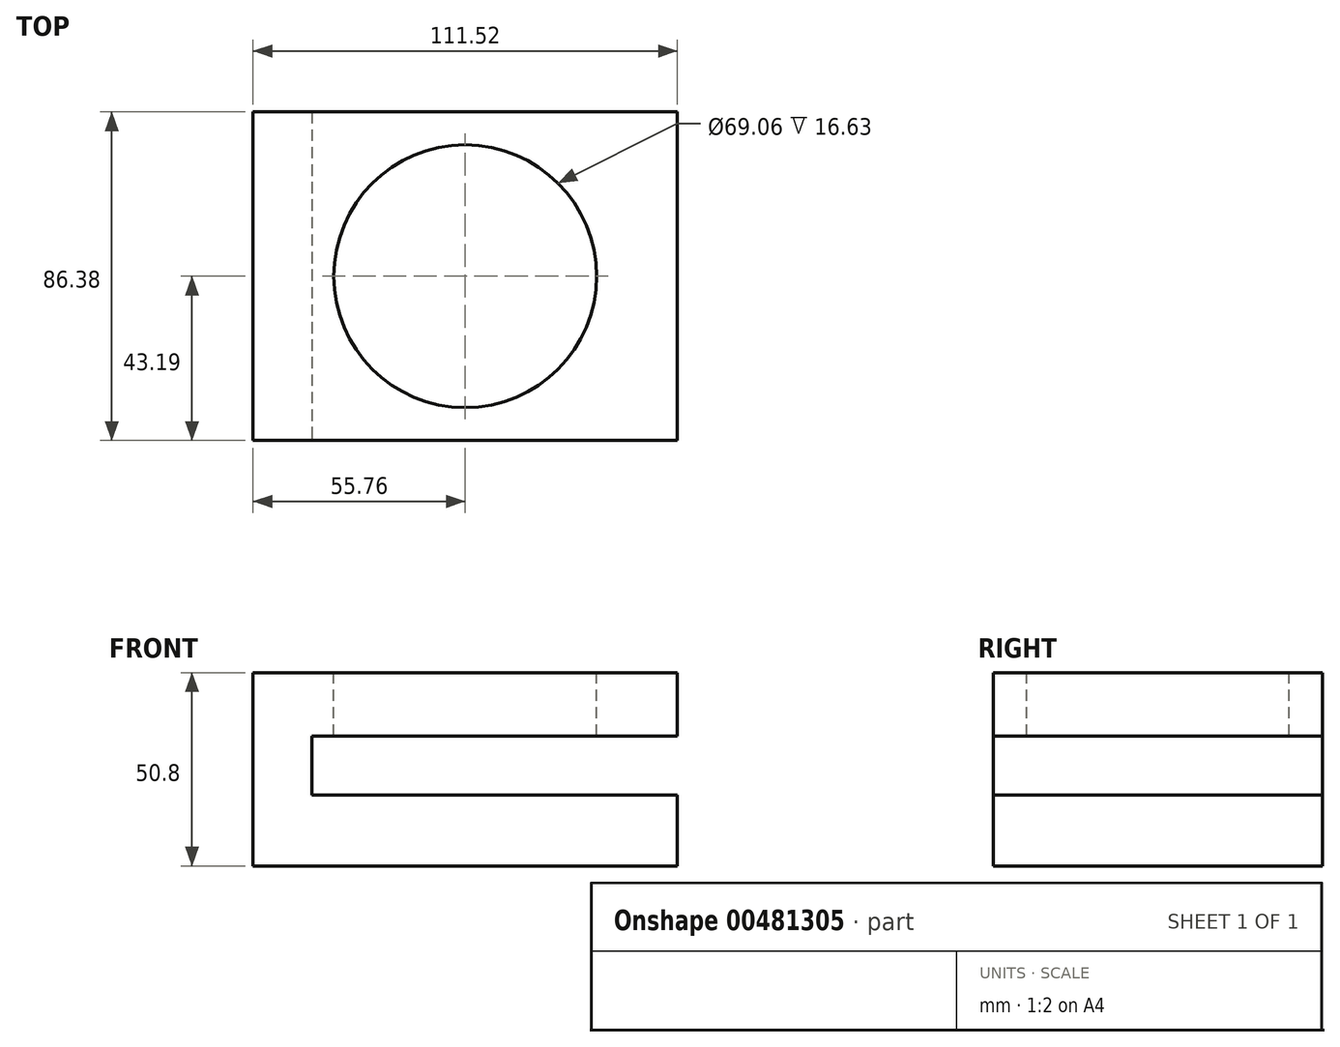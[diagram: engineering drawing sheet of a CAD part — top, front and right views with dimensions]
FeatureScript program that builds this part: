
annotation { "Feature Type Name" : "Feature", "Feature Type Description" : "" }
export const myFeature = defineFeature(function(context is Context, id is Id, definition is map)
    precondition{}
    {
        {
            var Q0;
            Q0=qCreatedBy(makeId("Top.planeOp"),FACE);
            var sketch = newSketch(context, id + "F0", { "sketchPlane" : qUnion([Q0])});
            skLineSegment(sketch, "E0.bottom", {"start": v(-55.76, -43.19) * mm, "end": v(55.76, -43.19) * mm});
            skLineSegment(sketch, "E0.top", {"start": v(-55.76, 43.19) * mm, "end": v(55.76, 43.19) * mm});
            skLineSegment(sketch, "E0.left", {"start": v(-55.76, -43.19) * mm, "end": v(-55.76, 43.19) * mm});
            skLineSegment(sketch, "E0.right", {"start": v(55.76, -43.19) * mm, "end": v(55.76, 43.19) * mm});
            skPoint(sketch, "E0.middle", {"position": v(0, 0) * mm});
            skSolve(sketch);
        }
        {
            var Q0;
            Q0=makeQuery(id+"F0.imprint","IMPRINT",FACE,{"disambiguationData":[TD([[makeQuery(id+"F0.imprint","IMPRINT",EDGE,{"derivedFrom":sQuery(id+"F0.wireOp",EDGE,"E0.bottom")}),1.0]])]});
            extrude(context, id + "F1", {"entities" : qUnion([Q0]), "oppositeDirection" : true, "depth" : 50.8 * mm});
        }
        {
            var Q0;
            Q0=makeQuery(id+"F1.opExtrude","SWEPT_FACE",FACE,{"disambiguationData":[OSD([sQuery(id+"F0.wireOp",EDGE,"E0.bottom")])]});
            var sketch = newSketch(context, id + "F2", { "sketchPlane" : qUnion([Q0])});
            skLineSegment(sketch, "E1.bottom", {"start": v(40.07, -11.57) * mm, "end": v(-40.07, -11.57) * mm});
            skLineSegment(sketch, "E1.top", {"start": v(40.07, -90.03) * mm, "end": v(-40.07, -90.03) * mm});
            skLineSegment(sketch, "E1.left", {"start": v(40.07, -11.57) * mm, "end": v(40.07, -90.03) * mm});
            skLineSegment(sketch, "E1.right", {"start": v(-40.07, -11.57) * mm, "end": v(-40.07, -90.03) * mm});
            skPoint(sketch, "E1.middle", {"position": v(0, -50.8) * mm});
            skSolve(sketch);
        }
        {
            var Q0;
            {var subQ0=sQuery(id+"F2.wireOp",EDGE,"E1.bottom");Q0=makeQuery(id+"F2.imprint","IMPRINT",FACE,{"disambiguationData":[TD([[makeQuery(id+"F2.imprint","IMPRINT",EDGE,{"derivedFrom":subQ0}),1.0]])]});}
            extrude(context, id + "F3", {"entities" : qUnion([Q0]), "operationType" : NewBodyOperationType.ADD, "oppositeDirection" : true, "depth" : 36.4 * mm});
        }
        {
            var Q0;
            Q0=makeQuery(id+"F1.opExtrude","SWEPT_FACE",FACE,{"disambiguationData":[OSD([sQuery(id+"F0.wireOp",EDGE,"E0.bottom")])]});
            var sketch = newSketch(context, id + "F4", { "sketchPlane" : qUnion([Q0])});
            skLineSegment(sketch, "E2.bottom", {"start": v(87.58, -32.15) * mm, "end": v(-40.28, -32.15) * mm});
            skLineSegment(sketch, "E2.top", {"start": v(87.58, -16.63) * mm, "end": v(-40.28, -16.63) * mm});
            skLineSegment(sketch, "E2.left", {"start": v(87.58, -32.15) * mm, "end": v(87.58, -16.63) * mm});
            skLineSegment(sketch, "E2.right", {"start": v(-40.28, -32.15) * mm, "end": v(-40.28, -16.63) * mm});
            skPoint(sketch, "E2.middle", {"position": v(23.65, -24.4) * mm});
            skSolve(sketch);
        }
        {
            var Q0;
            {var subQ0=sQuery(id+"F4.wireOp",EDGE,"E2.right");Q0=makeQuery(id+"F4.imprint","IMPRINT",FACE,{"disambiguationData":[TD([[makeQuery(id+"F4.imprint","IMPRINT",EDGE,{"derivedFrom":subQ0}),-1.0]])]});}
            extrude(context, id + "F5", {"entities" : qUnion([Q0]), "operationType" : NewBodyOperationType.REMOVE, "endBound" : BoundingType.THROUGH_ALL, "oppositeDirection" : true, "depth" : 25.4 * mm});
        }
        {
            var Q0;
            Q0=makeQuery(id+"F1.opExtrude","CAP_FACE",FACE,{"disambiguationData":[OSD([sQuery(id+"F0.wireOp",EDGE,"E0.bottom"),sQuery(id+"F0.wireOp",EDGE,"E0.top"),sQuery(id+"F0.wireOp",EDGE,"E0.left"),sQuery(id+"F0.wireOp",EDGE,"E0.right")])],"isStart":true});
            var sketch = newSketch(context, id + "F6", { "sketchPlane" : qUnion([Q0])});
            skCircle(sketch, "E3", {"center": v(0, 0) * mm, "radius": 34.53 * mm});
            skSolve(sketch);
        }
        {
            var Q0;
            Q0=makeQuery(id+"F6.imprint","IMPRINT",FACE,{"disambiguationData":[TD([[makeQuery(id+"F6.imprint","IMPRINT",EDGE,{"derivedFrom":sQuery(id+"F6.wireOp",EDGE,"E3")}),1.0]])]});
            extrude(context, id + "F7", {"entities" : qUnion([Q0]), "operationType" : NewBodyOperationType.REMOVE, "oppositeDirection" : true, "depth" : 25.4 * mm});
        }
    });
